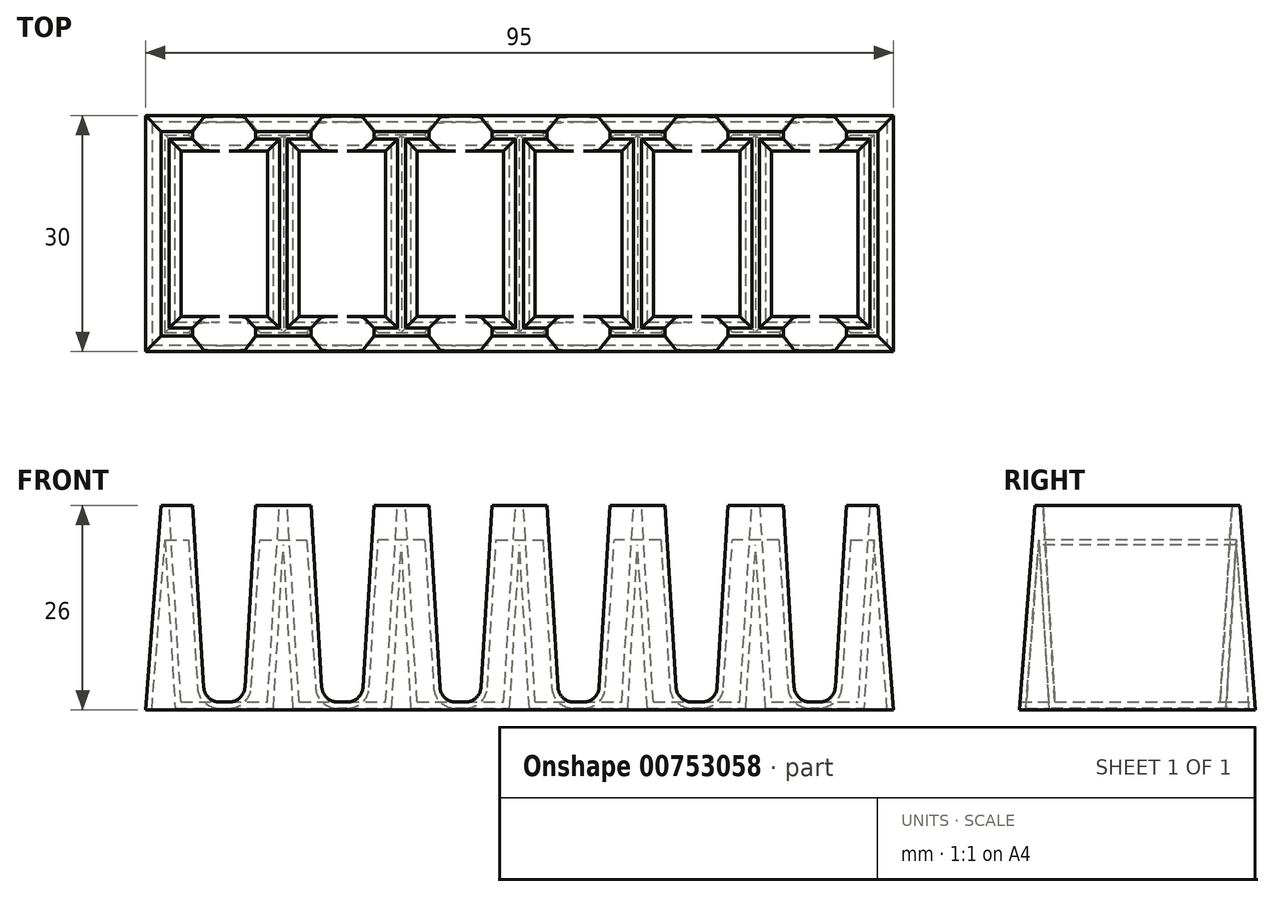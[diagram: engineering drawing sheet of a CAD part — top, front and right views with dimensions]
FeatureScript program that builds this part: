
annotation { "Feature Type Name" : "Feature", "Feature Type Description" : "" }
export const myFeature = defineFeature(function(context is Context, id is Id, definition is map)
    precondition{}
    {
        {
            var Q0;
            Q0=qCreatedBy(makeId("Right.planeOp"),FACE);
            var sketch = newSketch(context, id + "F0", { "sketchPlane" : qUnion([Q0])});
            skLineSegment(sketch, "E0.bottom", {"start": v(15, 0) * mm, "end": v(-15, 0) * mm});
            skLineSegment(sketch, "E0.top", {"start": v(13, 26) * mm, "end": v(-13, 26) * mm});
            skLineSegment(sketch, "E0.left", {"start": v(15, 0) * mm, "end": v(13, 26) * mm});
            skLineSegment(sketch, "E0.right", {"start": v(-15, 0) * mm, "end": v(-13, 26) * mm});
            skPoint(sketch, "E1", {"position": v(0, 26) * mm});
            skSolve(sketch);
        }
        {
            var Q0;
            Q0=makeQuery(id+"F0.imprint","IMPRINT",FACE,{"disambiguationData":[TD([[makeQuery(id+"F0.imprint","IMPRINT",EDGE,{"derivedFrom":sQuery(id+"F0.wireOp",EDGE,"E0.bottom")}),-1.0]])]});
            extrude(context, id + "F1", {"entities" : qUnion([Q0]), "depth" : 95 * mm, "offsetDistance" : 25 * mm});
        }
        {
            var Q0;
            Q0=qCreatedBy(makeId("Front.planeOp"),FACE);
            var sketch = newSketch(context, id + "F2", { "sketchPlane" : qUnion([Q0])});
            skLineSegment(sketch, "E2.0.0", {"start": v(0, 0) * mm, "end": v(0, 26) * mm});
            skLineSegment(sketch, "E2.0.1", {"start": v(0, 26) * mm, "end": v(95, 26) * mm});
            skLineSegment(sketch, "E2.0.2", {"start": v(95, 26) * mm, "end": v(95, 0) * mm});
            skLineSegment(sketch, "E2.0.3", {"start": v(95, 0) * mm, "end": v(0, 0) * mm});
            skLineSegment(sketch, "E3", {"start": v(0, 0) * mm, "end": v(2, 26) * mm});
            skLineSegment(sketch, "E4", {"start": v(95, 0) * mm, "end": v(93, 26) * mm});
            skLineSegment(sketch, "E5", {"start": v(93, 26) * mm, "end": v(95, 26) * mm});
            skLineSegment(sketch, "E6", {"start": v(2, 26) * mm, "end": v(0, 26) * mm});
            skLineSegment(sketch, "E7", {"start": v(-81.75, 44.93) * mm, "end": v(-86.9, 47.19) * mm});
            skSolve(sketch);
        }
        {
            var Q0;
            Q0=makeQuery(id+"F2.imprint","IMPRINT",FACE,{"disambiguationData":[TD([[makeQuery(id+"F2.imprint","IMPRINT",EDGE,{"derivedFrom":sQuery(id+"F2.wireOp",EDGE,"E2.0.0")}),-1.0]])]});
            var Q1;
            Q1=makeQuery(id+"F2.imprint","IMPRINT",FACE,{"disambiguationData":[TD([[makeQuery(id+"F2.imprint","IMPRINT",EDGE,{"derivedFrom":sQuery(id+"F2.wireOp",EDGE,"E2.0.2")}),-1.0]])]});
            extrude(context, id + "F3", {"entities" : qUnion([Q0, Q1]), "operationType" : NewBodyOperationType.REMOVE, "endBound" : BoundingType.SYMMETRIC, "oppositeDirection" : true, "depth" : 100 * mm, "offsetDistance" : 25 * mm});
        }
        {
            var Q0;
            Q0=qCreatedBy(makeId("Top.planeOp"),FACE);
            cPlane(context, id + "F4", {"entities" : qUnion([Q0]), "cplaneType" : CPlaneType.OFFSET, "offset" : 1 * mm, "width" : 150 * mm, "height" : 150 * mm});
        }
        {
            var Q0;
            Q0=qCreatedBy(id+"F4.planeOp",FACE);
            var sketch = newSketch(context, id + "F5", { "sketchPlane" : qUnion([Q0])});
            skLineSegment(sketch, "E8.0.0", {"start": v(0, -15) * mm, "end": v(0, 15) * mm});
            skLineSegment(sketch, "E8.0.1", {"start": v(0, 15) * mm, "end": v(95, 15) * mm});
            skLineSegment(sketch, "E8.0.2", {"start": v(95, 15) * mm, "end": v(95, -15) * mm});
            skLineSegment(sketch, "E8.0.3", {"start": v(95, -15) * mm, "end": v(0, -15) * mm});
            skLineSegment(sketch, "E9.bottom", {"start": v(4.5, -10.5) * mm, "end": v(15.5, -10.5) * mm});
            skLineSegment(sketch, "E9.top", {"start": v(4.5, 10.5) * mm, "end": v(15.5, 10.5) * mm});
            skLineSegment(sketch, "E9.left", {"start": v(4.5, -10.5) * mm, "end": v(4.5, 10.5) * mm});
            skLineSegment(sketch, "E9.right", {"start": v(15.5, -10.5) * mm, "end": v(15.5, 10.5) * mm});
            skLineSegment(sketch, "E10", {"start": v(0, 0) * mm, "end": v(51.63, 0) * mm, "construction": true});
            skLineSegment(sketch, "E11.1.0.0", {"start": v(30.5, -10.5) * mm, "end": v(30.5, 10.5) * mm});
            skLineSegment(sketch, "E11.1.0.1", {"start": v(19.5, -10.5) * mm, "end": v(30.5, -10.5) * mm});
            skLineSegment(sketch, "E11.1.0.2", {"start": v(19.5, -10.5) * mm, "end": v(19.5, 10.5) * mm});
            skLineSegment(sketch, "E11.1.0.3", {"start": v(19.5, 10.5) * mm, "end": v(30.5, 10.5) * mm});
            skLineSegment(sketch, "E11.2.0.0", {"start": v(45.5, -10.5) * mm, "end": v(45.5, 10.5) * mm});
            skLineSegment(sketch, "E11.2.0.1", {"start": v(34.5, -10.5) * mm, "end": v(45.5, -10.5) * mm});
            skLineSegment(sketch, "E11.2.0.2", {"start": v(34.5, -10.5) * mm, "end": v(34.5, 10.5) * mm});
            skLineSegment(sketch, "E11.2.0.3", {"start": v(34.5, 10.5) * mm, "end": v(45.5, 10.5) * mm});
            skLineSegment(sketch, "E11.3.0.0", {"start": v(60.5, -10.5) * mm, "end": v(60.5, 10.5) * mm});
            skLineSegment(sketch, "E11.3.0.1", {"start": v(49.5, -10.5) * mm, "end": v(60.5, -10.5) * mm});
            skLineSegment(sketch, "E11.3.0.2", {"start": v(49.5, -10.5) * mm, "end": v(49.5, 10.5) * mm});
            skLineSegment(sketch, "E11.3.0.3", {"start": v(49.5, 10.5) * mm, "end": v(60.5, 10.5) * mm});
            skLineSegment(sketch, "E11.direction1", {"start": v(15.5, -10.5) * mm, "end": v(30.5, -10.5) * mm, "construction": true});
            skLineSegment(sketch, "E12.0.4.0", {"start": v(75.5, -10.5) * mm, "end": v(75.5, 10.5) * mm});
            skLineSegment(sketch, "E12.3.4.0", {"start": v(64.5, -10.5) * mm, "end": v(75.5, -10.5) * mm});
            skLineSegment(sketch, "E12.6.4.0", {"start": v(64.5, -10.5) * mm, "end": v(64.5, 10.5) * mm});
            skLineSegment(sketch, "E12.9.4.0", {"start": v(64.5, 10.5) * mm, "end": v(75.5, 10.5) * mm});
            skLineSegment(sketch, "E12.0.5.0", {"start": v(90.5, -10.5) * mm, "end": v(90.5, 10.5) * mm});
            skLineSegment(sketch, "E12.3.5.0", {"start": v(79.5, -10.5) * mm, "end": v(90.5, -10.5) * mm});
            skLineSegment(sketch, "E12.6.5.0", {"start": v(79.5, -10.5) * mm, "end": v(79.5, 10.5) * mm});
            skLineSegment(sketch, "E12.9.5.0", {"start": v(79.5, 10.5) * mm, "end": v(90.5, 10.5) * mm});
            skSolve(sketch);
        }
        {
            var Q0;
            Q0=makeQuery(id+"F1.opExtrude","SWEPT_FACE",FACE,{"disambiguationData":[OSD([sQuery(id+"F0.wireOp",EDGE,"E0.top")])]});
            var sketch = newSketch(context, id + "F6", { "sketchPlane" : qUnion([Q0])});
            skLineSegment(sketch, "E13.0", {"start": v(95, 15) * mm, "end": v(95, -15) * mm});
            skLineSegment(sketch, "E13.1", {"start": v(0, 15) * mm, "end": v(95, 15) * mm});
            skLineSegment(sketch, "E13.2", {"start": v(0, -15) * mm, "end": v(0, 15) * mm});
            skLineSegment(sketch, "E13.3", {"start": v(95, -15) * mm, "end": v(0, -15) * mm});
            skLineSegment(sketch, "E14.0", {"start": v(0, 0) * mm, "end": v(51.63, 0) * mm, "construction": true});
            skLineSegment(sketch, "E15.bottom", {"start": v(3, 12) * mm, "end": v(17, 12) * mm});
            skLineSegment(sketch, "E15.top", {"start": v(3, -12) * mm, "end": v(17, -12) * mm});
            skLineSegment(sketch, "E15.left", {"start": v(3, 12) * mm, "end": v(3, -12) * mm});
            skLineSegment(sketch, "E15.right", {"start": v(17, 12) * mm, "end": v(17, -12) * mm});
            skLineSegment(sketch, "E16.0", {"start": v(2, 13) * mm, "end": v(2, -13) * mm, "construction": true});
            skLineSegment(sketch, "E17.0", {"start": v(4.5, -10.5) * mm, "end": v(4.5, 10.5) * mm, "construction": true});
            skLineSegment(sketch, "E18.1.0.0", {"start": v(18, 12) * mm, "end": v(18, -12) * mm});
            skLineSegment(sketch, "E18.1.0.1", {"start": v(18, 12) * mm, "end": v(32, 12) * mm});
            skLineSegment(sketch, "E18.1.0.2", {"start": v(32, 12) * mm, "end": v(32, -12) * mm});
            skLineSegment(sketch, "E18.1.0.3", {"start": v(18, -12) * mm, "end": v(32, -12) * mm});
            skLineSegment(sketch, "E18.2.0.0", {"start": v(33, 12) * mm, "end": v(33, -12) * mm});
            skLineSegment(sketch, "E18.2.0.1", {"start": v(33, 12) * mm, "end": v(47, 12) * mm});
            skLineSegment(sketch, "E18.2.0.2", {"start": v(47, 12) * mm, "end": v(47, -12) * mm});
            skLineSegment(sketch, "E18.2.0.3", {"start": v(33, -12) * mm, "end": v(47, -12) * mm});
            skLineSegment(sketch, "E18.3.0.0", {"start": v(48, 12) * mm, "end": v(48, -12) * mm});
            skLineSegment(sketch, "E18.3.0.1", {"start": v(48, 12) * mm, "end": v(62, 12) * mm});
            skLineSegment(sketch, "E18.3.0.2", {"start": v(62, 12) * mm, "end": v(62, -12) * mm});
            skLineSegment(sketch, "E18.3.0.3", {"start": v(48, -12) * mm, "end": v(62, -12) * mm});
            skLineSegment(sketch, "E18.direction1", {"start": v(3, -12) * mm, "end": v(18, -12) * mm, "construction": true});
            skLineSegment(sketch, "E19.0.4.0", {"start": v(63, 12) * mm, "end": v(63, -12) * mm});
            skLineSegment(sketch, "E19.3.4.0", {"start": v(63, 12) * mm, "end": v(77, 12) * mm});
            skLineSegment(sketch, "E19.6.4.0", {"start": v(77, 12) * mm, "end": v(77, -12) * mm});
            skLineSegment(sketch, "E19.9.4.0", {"start": v(63, -12) * mm, "end": v(77, -12) * mm});
            skLineSegment(sketch, "E19.0.5.0", {"start": v(78, 12) * mm, "end": v(78, -12) * mm});
            skLineSegment(sketch, "E19.3.5.0", {"start": v(78, 12) * mm, "end": v(92, 12) * mm});
            skLineSegment(sketch, "E19.6.5.0", {"start": v(92, 12) * mm, "end": v(92, -12) * mm});
            skLineSegment(sketch, "E19.9.5.0", {"start": v(78, -12) * mm, "end": v(92, -12) * mm});
            skSolve(sketch);
        }
        {
            var Q1;
            Q1=makeQuery(id+"F5.imprint","IMPRINT",FACE,{"disambiguationData":[TD([[makeQuery(id+"F5.imprint","IMPRINT",EDGE,{"derivedFrom":sQuery(id+"F5.wireOp",EDGE,"E9.bottom")}),1.0]])]});
            var Q2;
            Q2=makeQuery(id+"F6.imprint","IMPRINT",FACE,{"disambiguationData":[TD([[makeQuery(id+"F6.imprint","IMPRINT",EDGE,{"derivedFrom":sQuery(id+"F6.wireOp",EDGE,"E15.bottom")}),-1.0]])]});
            loft(context, id + "F7", {"operationType" : NewBodyOperationType.REMOVE, "sheetProfilesArray" : [{ "sheetProfileEntities" : qUnion([Q1]) }, { "sheetProfileEntities" : qUnion([Q2]) }]});
        }
        {
            var Q1;
            Q1=makeQuery(id+"F5.imprint","IMPRINT",FACE,{"disambiguationData":[TD([[makeQuery(id+"F5.imprint","IMPRINT",EDGE,{"derivedFrom":sQuery(id+"F5.wireOp",EDGE,"E11.1.0.0")}),1.0]])]});
            var Q2;
            Q2=makeQuery(id+"F6.imprint","IMPRINT",FACE,{"disambiguationData":[TD([[makeQuery(id+"F6.imprint","IMPRINT",EDGE,{"derivedFrom":sQuery(id+"F6.wireOp",EDGE,"E18.1.0.0")}),1.0]])]});
            loft(context, id + "F8", {"operationType" : NewBodyOperationType.REMOVE, "sheetProfilesArray" : [{ "sheetProfileEntities" : qUnion([Q1]) }, { "sheetProfileEntities" : qUnion([Q2]) }]});
        }
        {
            var Q1;
            Q1=makeQuery(id+"F5.imprint","IMPRINT",FACE,{"disambiguationData":[TD([[makeQuery(id+"F5.imprint","IMPRINT",EDGE,{"derivedFrom":sQuery(id+"F5.wireOp",EDGE,"E11.2.0.0")}),1.0]])]});
            var Q2;
            Q2=makeQuery(id+"F6.imprint","IMPRINT",FACE,{"disambiguationData":[TD([[makeQuery(id+"F6.imprint","IMPRINT",EDGE,{"derivedFrom":sQuery(id+"F6.wireOp",EDGE,"E18.2.0.0")}),1.0]])]});
            loft(context, id + "F9", {"operationType" : NewBodyOperationType.REMOVE, "sheetProfilesArray" : [{ "sheetProfileEntities" : qUnion([Q1]) }, { "sheetProfileEntities" : qUnion([Q2]) }]});
        }
        {
            var Q1;
            Q1=makeQuery(id+"F5.imprint","IMPRINT",FACE,{"disambiguationData":[TD([[makeQuery(id+"F5.imprint","IMPRINT",EDGE,{"derivedFrom":sQuery(id+"F5.wireOp",EDGE,"E11.3.0.0")}),1.0]])]});
            var Q2;
            Q2=makeQuery(id+"F6.imprint","IMPRINT",FACE,{"disambiguationData":[TD([[makeQuery(id+"F6.imprint","IMPRINT",EDGE,{"derivedFrom":sQuery(id+"F6.wireOp",EDGE,"E18.3.0.0")}),1.0]])]});
            loft(context, id + "F10", {"operationType" : NewBodyOperationType.REMOVE, "sheetProfilesArray" : [{ "sheetProfileEntities" : qUnion([Q1]) }, { "sheetProfileEntities" : qUnion([Q2]) }]});
        }
        {
            var Q1;
            Q1=makeQuery(id+"F5.imprint","IMPRINT",FACE,{"disambiguationData":[TD([[makeQuery(id+"F5.imprint","IMPRINT",EDGE,{"derivedFrom":sQuery(id+"F5.wireOp",EDGE,"E12.0.4.0")}),1.0]])]});
            var Q2;
            Q2=makeQuery(id+"F6.imprint","IMPRINT",FACE,{"disambiguationData":[TD([[makeQuery(id+"F6.imprint","IMPRINT",EDGE,{"derivedFrom":sQuery(id+"F6.wireOp",EDGE,"E19.0.4.0")}),1.0]])]});
            loft(context, id + "F11", {"operationType" : NewBodyOperationType.REMOVE, "sheetProfilesArray" : [{ "sheetProfileEntities" : qUnion([Q1]) }, { "sheetProfileEntities" : qUnion([Q2]) }]});
        }
        {
            var Q1;
            Q1=makeQuery(id+"F6.imprint","IMPRINT",FACE,{"disambiguationData":[TD([[makeQuery(id+"F6.imprint","IMPRINT",EDGE,{"derivedFrom":sQuery(id+"F6.wireOp",EDGE,"E19.0.5.0")}),1.0]])]});
            var Q2;
            Q2=makeQuery(id+"F5.imprint","IMPRINT",FACE,{"disambiguationData":[TD([[makeQuery(id+"F5.imprint","IMPRINT",EDGE,{"derivedFrom":sQuery(id+"F5.wireOp",EDGE,"E12.0.5.0")}),1.0]])]});
            loft(context, id + "F12", {"operationType" : NewBodyOperationType.REMOVE, "sheetProfilesArray" : [{ "sheetProfileEntities" : qUnion([Q1]) }, { "sheetProfileEntities" : qUnion([Q2]) }]});
        }
        {
            var Q0;
            Q0=qCreatedBy(makeId("Front.planeOp"),FACE);
            var sketch = newSketch(context, id + "F13", { "sketchPlane" : qUnion([Q0])});
            skPoint(sketch, "E20.1", {"position": v(4.5, 1) * mm});
            skPoint(sketch, "E20.2", {"position": v(15.5, 1) * mm});
            skPoint(sketch, "E20.3", {"position": v(17, 26) * mm});
            skLineSegment(sketch, "E21", {"start": v(15.5, 1) * mm, "end": v(17, 26) * mm, "construction": true});
            skLineSegment(sketch, "E22", {"start": v(15.5, 1) * mm, "end": v(4.5, 1) * mm});
            skLineSegment(sketch, "E23", {"start": v(10.62, 1) * mm, "end": v(4.5, 1) * mm});
            skPoint(sketch, "E24.0", {"position": v(3, 26) * mm});
            skLineSegment(sketch, "E25", {"start": v(3, 26) * mm, "end": v(17, 26) * mm, "construction": true});
            skLineSegment(sketch, "E26", {"start": v(3, 26) * mm, "end": v(4.5, 1) * mm, "construction": true});
            skLineSegment(sketch, "E27", {"start": v(10, 26) * mm, "end": v(10, 1) * mm, "construction": true});
            skLineSegment(sketch, "E28", {"start": v(6, 26) * mm, "end": v(14, 26) * mm});
            skLineSegment(sketch, "E29", {"start": v(7.39, 2.88) * mm, "end": v(6, 26) * mm});
            skLineSegment(sketch, "E30", {"start": v(14, 26) * mm, "end": v(12.61, 2.88) * mm});
            skLineSegment(sketch, "E31", {"start": v(11.5, 1) * mm, "end": v(18.5, 1) * mm});
            skArc(sketch, "E32.filletArc", {"start": v(7.39, 2.88) * mm, "mid": v(8.01, 1.54) * mm, "end": v(9.38, 1) * mm});
            skArc(sketch, "E33.filletArc", {"start": v(10.62, 1) * mm, "mid": v(11.99, 1.54) * mm, "end": v(12.61, 2.88) * mm});
            skLineSegment(sketch, "E34", {"start": v(9.38, 1) * mm, "end": v(10.62, 1) * mm});
            skLineSegment(sketch, "E35.1.0.0", {"start": v(29, 26) * mm, "end": v(27.61, 2.88) * mm});
            skArc(sketch, "E35.1.0.1", {"start": v(22.39, 2.88) * mm, "mid": v(23.01, 1.54) * mm, "end": v(24.38, 1) * mm});
            skLineSegment(sketch, "E35.1.0.2", {"start": v(22.39, 2.88) * mm, "end": v(21, 26) * mm});
            skLineSegment(sketch, "E35.1.0.3", {"start": v(21, 26) * mm, "end": v(29, 26) * mm});
            skArc(sketch, "E35.1.0.4", {"start": v(25.62, 1) * mm, "mid": v(26.99, 1.54) * mm, "end": v(27.61, 2.88) * mm});
            skPoint(sketch, "E35.1.0.5", {"position": v(19.5, 1) * mm});
            skLineSegment(sketch, "E35.1.0.6", {"start": v(25, 26) * mm, "end": v(25, 1) * mm, "construction": true});
            skLineSegment(sketch, "E35.1.0.7", {"start": v(24.38, 1) * mm, "end": v(25.62, 1) * mm});
            skLineSegment(sketch, "E35.1.0.8", {"start": v(24.38, 1) * mm, "end": v(25.62, 1) * mm});
            skLineSegment(sketch, "E35.2.0.0", {"start": v(44, 26) * mm, "end": v(42.61, 2.88) * mm});
            skArc(sketch, "E35.2.0.1", {"start": v(37.39, 2.88) * mm, "mid": v(38.01, 1.54) * mm, "end": v(39.38, 1) * mm});
            skLineSegment(sketch, "E35.2.0.2", {"start": v(37.39, 2.88) * mm, "end": v(36, 26) * mm});
            skLineSegment(sketch, "E35.2.0.3", {"start": v(36, 26) * mm, "end": v(44, 26) * mm});
            skArc(sketch, "E35.2.0.4", {"start": v(40.62, 1) * mm, "mid": v(41.99, 1.54) * mm, "end": v(42.61, 2.88) * mm});
            skPoint(sketch, "E35.2.0.5", {"position": v(34.5, 1) * mm});
            skLineSegment(sketch, "E35.2.0.6", {"start": v(40, 26) * mm, "end": v(40, 1) * mm, "construction": true});
            skLineSegment(sketch, "E35.2.0.7", {"start": v(39.38, 1) * mm, "end": v(40.62, 1) * mm});
            skLineSegment(sketch, "E35.2.0.8", {"start": v(39.38, 1) * mm, "end": v(40.62, 1) * mm});
            skLineSegment(sketch, "E35.3.0.0", {"start": v(59, 26) * mm, "end": v(57.61, 2.88) * mm});
            skArc(sketch, "E35.3.0.1", {"start": v(52.39, 2.88) * mm, "mid": v(53.01, 1.54) * mm, "end": v(54.38, 1) * mm});
            skLineSegment(sketch, "E35.3.0.2", {"start": v(52.39, 2.88) * mm, "end": v(51, 26) * mm});
            skLineSegment(sketch, "E35.3.0.3", {"start": v(51, 26) * mm, "end": v(59, 26) * mm});
            skArc(sketch, "E35.3.0.4", {"start": v(55.62, 1) * mm, "mid": v(56.99, 1.54) * mm, "end": v(57.61, 2.88) * mm});
            skPoint(sketch, "E35.3.0.5", {"position": v(49.5, 1) * mm});
            skLineSegment(sketch, "E35.3.0.6", {"start": v(55, 26) * mm, "end": v(55, 1) * mm, "construction": true});
            skLineSegment(sketch, "E35.3.0.7", {"start": v(54.38, 1) * mm, "end": v(55.62, 1) * mm});
            skLineSegment(sketch, "E35.3.0.8", {"start": v(54.38, 1) * mm, "end": v(55.62, 1) * mm});
            skLineSegment(sketch, "E35.4.0.0", {"start": v(74, 26) * mm, "end": v(72.61, 2.88) * mm});
            skArc(sketch, "E35.4.0.1", {"start": v(67.39, 2.88) * mm, "mid": v(68.01, 1.54) * mm, "end": v(69.38, 1) * mm});
            skLineSegment(sketch, "E35.4.0.2", {"start": v(67.39, 2.88) * mm, "end": v(66, 26) * mm});
            skLineSegment(sketch, "E35.4.0.3", {"start": v(66, 26) * mm, "end": v(74, 26) * mm});
            skArc(sketch, "E35.4.0.4", {"start": v(70.62, 1) * mm, "mid": v(71.99, 1.54) * mm, "end": v(72.61, 2.88) * mm});
            skPoint(sketch, "E35.4.0.5", {"position": v(64.5, 1) * mm});
            skLineSegment(sketch, "E35.4.0.6", {"start": v(70, 26) * mm, "end": v(70, 1) * mm, "construction": true});
            skLineSegment(sketch, "E35.4.0.7", {"start": v(69.38, 1) * mm, "end": v(70.62, 1) * mm});
            skLineSegment(sketch, "E35.4.0.8", {"start": v(69.38, 1) * mm, "end": v(70.62, 1) * mm});
            skLineSegment(sketch, "E35.5.0.0", {"start": v(89, 26) * mm, "end": v(87.61, 2.88) * mm});
            skArc(sketch, "E35.5.0.1", {"start": v(82.39, 2.88) * mm, "mid": v(83.01, 1.54) * mm, "end": v(84.38, 1) * mm});
            skLineSegment(sketch, "E35.5.0.2", {"start": v(82.39, 2.88) * mm, "end": v(81, 26) * mm});
            skLineSegment(sketch, "E35.5.0.3", {"start": v(81, 26) * mm, "end": v(89, 26) * mm});
            skArc(sketch, "E35.5.0.4", {"start": v(85.62, 1) * mm, "mid": v(86.99, 1.54) * mm, "end": v(87.61, 2.88) * mm});
            skPoint(sketch, "E35.5.0.5", {"position": v(79.5, 1) * mm});
            skLineSegment(sketch, "E35.5.0.6", {"start": v(85, 26) * mm, "end": v(85, 1) * mm, "construction": true});
            skLineSegment(sketch, "E35.5.0.7", {"start": v(84.38, 1) * mm, "end": v(85.62, 1) * mm});
            skLineSegment(sketch, "E35.5.0.8", {"start": v(84.38, 1) * mm, "end": v(85.62, 1) * mm});
            skLineSegment(sketch, "E35.direction1", {"start": v(4.5, 1) * mm, "end": v(19.5, 1) * mm, "construction": true});
            skSolve(sketch);
        }
        {
            var Q0;
            Q0=makeQuery(id+"F13.imprint","IMPRINT",FACE,{"disambiguationData":[TD([[makeQuery(id+"F13.imprint","IMPRINT",EDGE,{"derivedFrom":sQuery(id+"F13.wireOp",EDGE,"E28")}),-1.0]])]});
            var Q1;
            Q1=makeQuery(id+"F13.imprint","IMPRINT",FACE,{"disambiguationData":[TD([[makeQuery(id+"F13.imprint","IMPRINT",EDGE,{"derivedFrom":sQuery(id+"F13.wireOp",EDGE,"8a8e7ac3-a0b8-4f3d-88e1-f5d4d7c65634.1.0.1")}),-1.0]])]});
            var Q2;
            Q2=makeQuery(id+"F13.imprint","IMPRINT",FACE,{"disambiguationData":[TD([[makeQuery(id+"F13.imprint","IMPRINT",EDGE,{"derivedFrom":sQuery(id+"F13.wireOp",EDGE,"8a8e7ac3-a0b8-4f3d-88e1-f5d4d7c65634.2.0.1")}),-1.0]])]});
            var Q3;
            Q3=makeQuery(id+"F13.imprint","IMPRINT",FACE,{"disambiguationData":[TD([[makeQuery(id+"F13.imprint","IMPRINT",EDGE,{"derivedFrom":sQuery(id+"F13.wireOp",EDGE,"8a8e7ac3-a0b8-4f3d-88e1-f5d4d7c65634.3.0.1")}),-1.0]])]});
            var Q4;
            Q4=makeQuery(id+"F13.imprint","IMPRINT",FACE,{"disambiguationData":[TD([[makeQuery(id+"F13.imprint","IMPRINT",EDGE,{"derivedFrom":sQuery(id+"F13.wireOp",EDGE,"E35.1.0.0")}),-1.0]])]});
            var Q5;
            Q5=makeQuery(id+"F13.imprint","IMPRINT",FACE,{"disambiguationData":[TD([[makeQuery(id+"F13.imprint","IMPRINT",EDGE,{"derivedFrom":sQuery(id+"F13.wireOp",EDGE,"E35.2.0.0")}),-1.0]])]});
            var Q6;
            Q6=makeQuery(id+"F13.imprint","IMPRINT",FACE,{"disambiguationData":[TD([[makeQuery(id+"F13.imprint","IMPRINT",EDGE,{"derivedFrom":sQuery(id+"F13.wireOp",EDGE,"E35.3.0.0")}),-1.0]])]});
            var Q7;
            Q7=makeQuery(id+"F13.imprint","IMPRINT",FACE,{"disambiguationData":[TD([[makeQuery(id+"F13.imprint","IMPRINT",EDGE,{"derivedFrom":sQuery(id+"F13.wireOp",EDGE,"E35.4.0.0")}),-1.0]])]});
            var Q8;
            Q8=makeQuery(id+"F13.imprint","IMPRINT",FACE,{"disambiguationData":[TD([[makeQuery(id+"F13.imprint","IMPRINT",EDGE,{"derivedFrom":sQuery(id+"F13.wireOp",EDGE,"E35.5.0.0")}),-1.0]])]});
            extrude(context, id + "F14", {"entities" : qUnion([Q0, Q1, Q2, Q3, Q4, Q5, Q6, Q7, Q8]), "operationType" : NewBodyOperationType.REMOVE, "endBound" : BoundingType.SYMMETRIC, "depth" : 50 * mm, "offsetDistance" : 25 * mm});
        }
        {
            var Q0;
            Q0=makeQuery(id+"F1.opExtrude","SWEPT_FACE",FACE,{"disambiguationData":[OSD([sQuery(id+"F0.wireOp",EDGE,"E0.bottom")])]});
            shell(context, id + "F15", {"entities" : qUnion([Q0]), "thickness" : 0.8 * mm});
        }
    });
